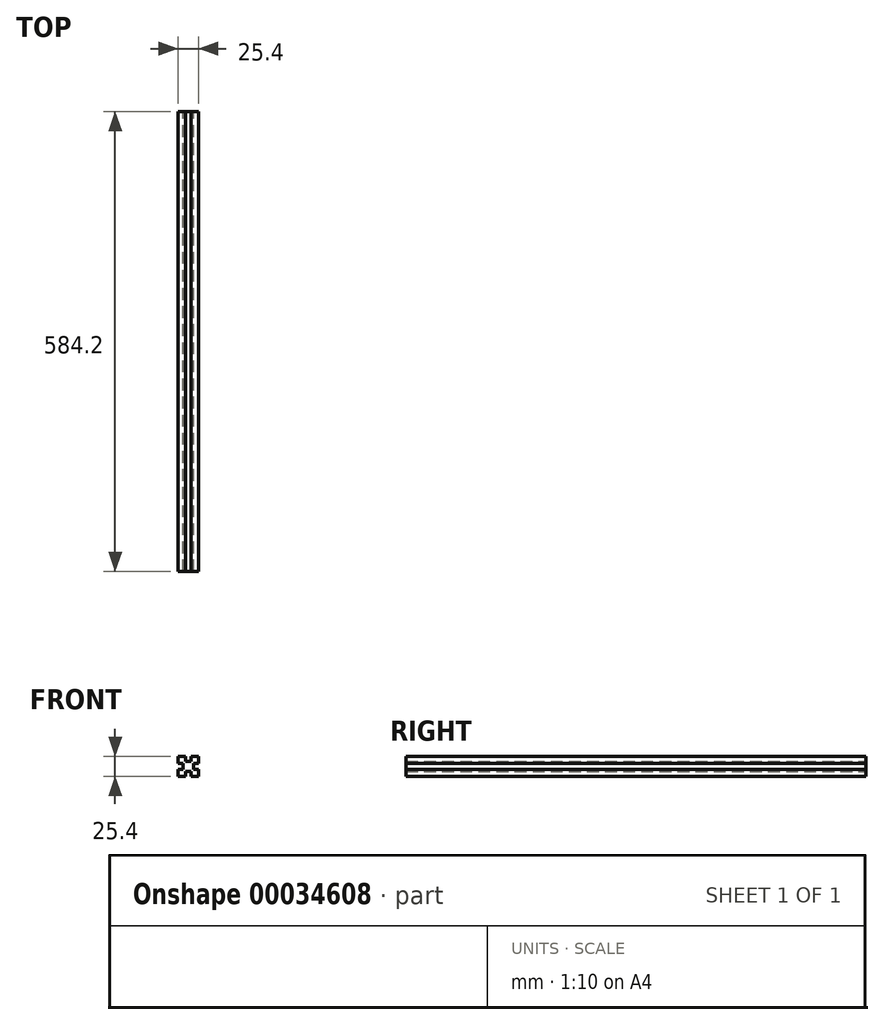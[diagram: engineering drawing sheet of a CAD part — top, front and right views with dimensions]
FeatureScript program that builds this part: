
annotation { "Feature Type Name" : "Feature", "Feature Type Description" : "" }
export const myFeature = defineFeature(function(context is Context, id is Id, definition is map)
    precondition{}
    {
        {
            var Q0;
            Q0=qCreatedBy(makeId("Front.planeOp"),FACE);
            var sketch = newSketch(context, id + "F0", { "sketchPlane" : qUnion([Q0])});
            skLineSegment(sketch, "E0.bottom", {"start": v(0, 0) * mm, "end": v(8.9, 0) * mm});
            skLineSegment(sketch, "E0.top", {"start": v(0, 25.4) * mm, "end": v(8.89, 25.4) * mm});
            skLineSegment(sketch, "E0.left", {"start": v(0, 0) * mm, "end": v(0, 8.9) * mm});
            skLineSegment(sketch, "E0.right", {"start": v(25.4, 0) * mm, "end": v(25.4, 8.89) * mm});
            skLineSegment(sketch, "E1.top", {"start": v(8.89, 19.05) * mm, "end": v(16.51, 19.05) * mm});
            skLineSegment(sketch, "E1.left", {"start": v(8.89, 25.4) * mm, "end": v(8.89, 19.05) * mm});
            skLineSegment(sketch, "E1.right", {"start": v(16.51, 25.4) * mm, "end": v(16.51, 19.05) * mm});
            skLineSegment(sketch, "E2.bottom", {"start": v(0, 16.5) * mm, "end": v(6.35, 16.5) * mm});
            skLineSegment(sketch, "E2.top", {"start": v(0, 8.9) * mm, "end": v(6.35, 8.9) * mm});
            skLineSegment(sketch, "E2.right", {"start": v(6.35, 16.5) * mm, "end": v(6.35, 8.9) * mm});
            skLineSegment(sketch, "E3.bottom", {"start": v(8.89, 6.35) * mm, "end": v(16.5, 6.35) * mm});
            skLineSegment(sketch, "E3.left", {"start": v(8.9, 6.35) * mm, "end": v(8.9, 0) * mm});
            skLineSegment(sketch, "E3.right", {"start": v(16.5, 6.35) * mm, "end": v(16.5, 0) * mm});
            skLineSegment(sketch, "E4.bottom", {"start": v(19.05, 16.5) * mm, "end": v(25.4, 16.5) * mm});
            skLineSegment(sketch, "E4.top", {"start": v(19.05, 8.89) * mm, "end": v(25.4, 8.89) * mm});
            skLineSegment(sketch, "E4.left", {"start": v(19.05, 16.5) * mm, "end": v(19.05, 8.89) * mm});
            skLineSegment(sketch, "E5.trimOffspring", {"start": v(0, 16.5) * mm, "end": v(0, 25.4) * mm});
            skLineSegment(sketch, "E6.trimOffspring", {"start": v(25.4, 16.5) * mm, "end": v(25.4, 25.4) * mm});
            skLineSegment(sketch, "E7.trimOffspring", {"start": v(16.5, 0) * mm, "end": v(25.4, 0) * mm});
            skLineSegment(sketch, "E8.trimOffspring", {"start": v(16.51, 25.4) * mm, "end": v(25.4, 25.4) * mm});
            skSolve(sketch);
        }
        {
            var Q0;
            Q0 = qSketchRegion(id + "F0", true);
            extrude(context, id + "F1", {"entities" : qUnion([Q0]), "depth" : 584.2 * mm});
        }
    });
